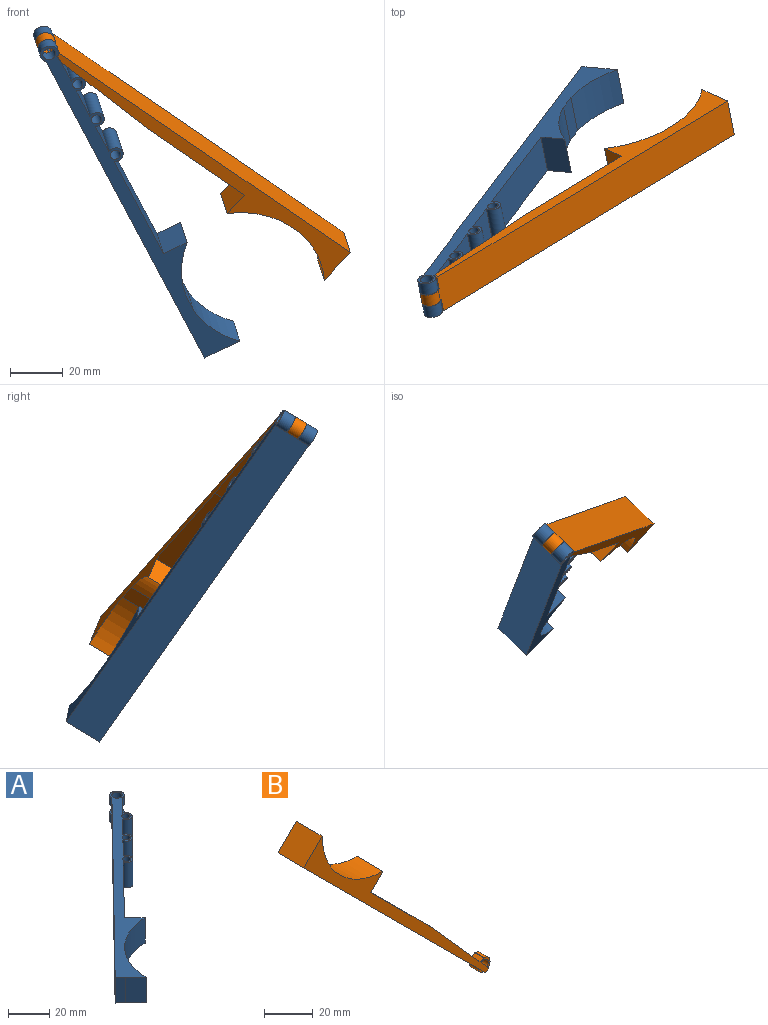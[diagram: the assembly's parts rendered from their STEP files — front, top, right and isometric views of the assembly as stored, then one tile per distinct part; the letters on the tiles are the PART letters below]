
ASSEMBLY  parts=2 mates=1
PART A: 26 faces, bbox 112x121.2x15 mm
  f0: plane 121.16x111.96mm, normal (0,0,-1), area 945.2mm2, adj f1,f2,f5,f7,f8,f9,f10,f11
  f1: plane 15x5.03mm, normal (0.71,-0.7,0), area 105.5mm2, adj f0,f6,f19,f21
  f2: plane 15x0.04mm, normal (0.71,-0.7,0), area 0.8mm2, adj f0,f6,f8,f20
  f3: plane 5.06x1.43mm, normal (0.7,0.71,0), area 10.1mm2, adj f7,f16,f17,f18
  f4: plane 5.06x1.43mm, normal (0.7,0.71,0), area 10.1mm2, adj f5,f16,f17,f18
  f5: cylinder r=3.5mm len=15mm, axis (0,0,-1), area 164.3mm2, adj f0,f4,f6,f7,f15,f16,f17
  f6: plane 121.16x111.96mm, normal (0,0,1), area 945.2mm2, adj f1,f2,f5,f7,f8,f9,f10,f11
  f7: plane 107.16x104.96mm, normal (-0.71,0.7,0), area 2250mm2, adj f0,f3,f5,f6,f8
  f8: plane 15x3.54mm, normal (-0.71,-0.71,0), area 75mm2, adj f0,f2,f6,f7
  f9: plane 33.35x32.65mm, normal (0.71,-0.7,0), area 700.1mm2, adj f0,f6,f10,f22
  f10: cylinder r=3mm len=15mm, axis (0,0,-1), area 194.1mm2, adj f0,f6,f9,f11
  f11: plane 15x9.2mm, normal (0.71,-0.7,0), area 193mm2, adj f0,f6,f10,f12
  f12: cylinder r=3mm len=15mm, axis (0,0,-1), area 194.1mm2, adj f0,f6,f11,f13
  f13: plane 15x9.2mm, normal (0.71,-0.7,0), area 193mm2, adj f0,f6,f12,f14
  f14: cylinder r=3mm len=15mm, axis (0,0,-1), area 194.1mm2, adj f0,f6,f13,f15
  f15: plane 15x9mm, normal (0.71,-0.7,0), area 188.9mm2, adj f0,f5,f6,f14
  f16: plane 7x7mm, normal (0,0,-1), area 15.3mm2, adj f3,f4,f5,f18
  f17: plane 7x7mm, normal (0,0,1), area 15.3mm2, adj f3,f4,f5,f18
  f18: cylinder r=2.5mm len=15mm, axis (0,0,-1), area 161.3mm2, adj f0,f3,f4,f6,f16,f17
  f19: cylinder r=35.72mm len=22.32mm, axis (0,0,1), area 361.8mm2, adj f0,f1,f6,f20
  f20: plane 15x7.14mm, normal (-0.7,-0.71,0), area 150mm2, adj f0,f2,f6,f19
  f21: cylinder r=35.72mm len=22.17mm, axis (0,0,1), area 362.2mm2, adj f0,f1,f6,f22
  f22: plane 15x7.16mm, normal (0.7,0.71,0), area 150.3mm2, adj f0,f6,f9,f21
  f23: cylinder r=2mm len=15mm, axis (0,0,-1), area 188.5mm2, adj f0,f6
  f24: cylinder r=2mm len=15mm, axis (0,0,-1), area 188.5mm2, adj f0,f6
  f25: cylinder r=2mm len=15mm, axis (0,0,-1), area 188.5mm2, adj f0,f6
PART B: 23 faces, bbox 113.1x15x120.1 mm
  f0: plane 15x5.23mm, normal (0.71,0,0.71), area 110.9mm2, adj f8,f9,f19,f21
  f1: plane 7.35x7.35mm, normal (0,1,0), area 17.3mm2, adj f2,f3,f5,f6,f7,f10,f12,f16
  f2: plane 5x0.64mm, normal (-0.71,0,0.71), area 4.5mm2, adj f1,f11,f15,f17
  f3: plane 5x0.01mm, normal (-0.71,0,0.71), area 0.1mm2, adj f1,f10,f11,f18
  f4: plane 35.01x35mm, normal (0.71,0,0.71), area 742.5mm2, adj f8,f9,f14,f22
  f5: plane 5x1.33mm, normal (0.71,0,-0.71), area 9.4mm2, adj f1,f7,f9,f15
  f6: cylinder r=3.5mm len=7mm, axis (0,1,0), area 82.5mm2, adj f1,f7,f10,f11
  f7: plane 106.12x106.01mm, normal (-0.71,0,-0.71), area 2245mm2, adj f1,f5,f6,f8,f9,f11,f13,f20
  f8: plane 116.27x107.1mm, normal (0,-1,0), area 825.8mm2, adj f0,f4,f7,f13,f14,f15,f19,f20
  f9: plane 116.27x107.1mm, normal (0,1,0), area 825.8mm2, adj f0,f4,f5,f7,f14,f15,f19,f20
  f10: plane 5x0.35mm, normal (0.71,0,0.71), area 2.5mm2, adj f1,f3,f6,f11
  f11: plane 7.35x7.35mm, normal (0,-1,0), area 17.3mm2, adj f2,f3,f6,f7,f10,f12,f13,f16
  f12: cylinder r=2.5mm len=5mm, axis (0,-1,0), area 75mm2, adj f1,f11,f16
  f13: plane 5x1.33mm, normal (0.71,0,-0.71), area 9.4mm2, adj f7,f8,f11,f15
  f14: plane 34.28x30.78mm, normal (0.74,0,0.67), area 691mm2, adj f4,f8,f9,f15
  f15: plane 15x3.24mm, normal (0.8,0,0.6), area 60.6mm2, adj f2,f5,f8,f9,f13,f14
  f16: plane 5x0.5mm, normal (0.71,0,-0.71), area 3.6mm2, adj f1,f11,f12
  f17: plane 5x1.84mm, normal (-0.54,0,0.84), area 11mm2, adj f1,f2,f11,f18
  f18: plane 5x0.33mm, normal (-0.71,0,-0.7), area 2.3mm2, adj f1,f3,f11,f17
  f19: cylinder r=35.74mm len=22.13mm, axis (0,-1,0), area 359.6mm2, adj f0,f8,f9,f20
  f20: plane 15x10.61mm, normal (-0.71,0,0.71), area 225mm2, adj f7,f8,f9,f19
  f21: cylinder r=35.74mm len=22.15mm, axis (0,-1,0), area 360mm2, adj f0,f8,f9,f22
  f22: plane 15x7.08mm, normal (0.71,0,-0.71), area 150.3mm2, adj f4,f8,f9,f21
PLACE A rot(axis=(0.8,-0.49,0.36),137.1deg) t=(6.93,-6.57,83.89)mm
PLACE B rot(axis=(-0.07,0.96,0.27),174.2deg) t=(6.93,-6.57,83.89)mm fixed
MATE revolute B.f6 <-> A.f5  axis (-0.17,0.85,0.51) through (8.18,-12.91,80.08)mm
